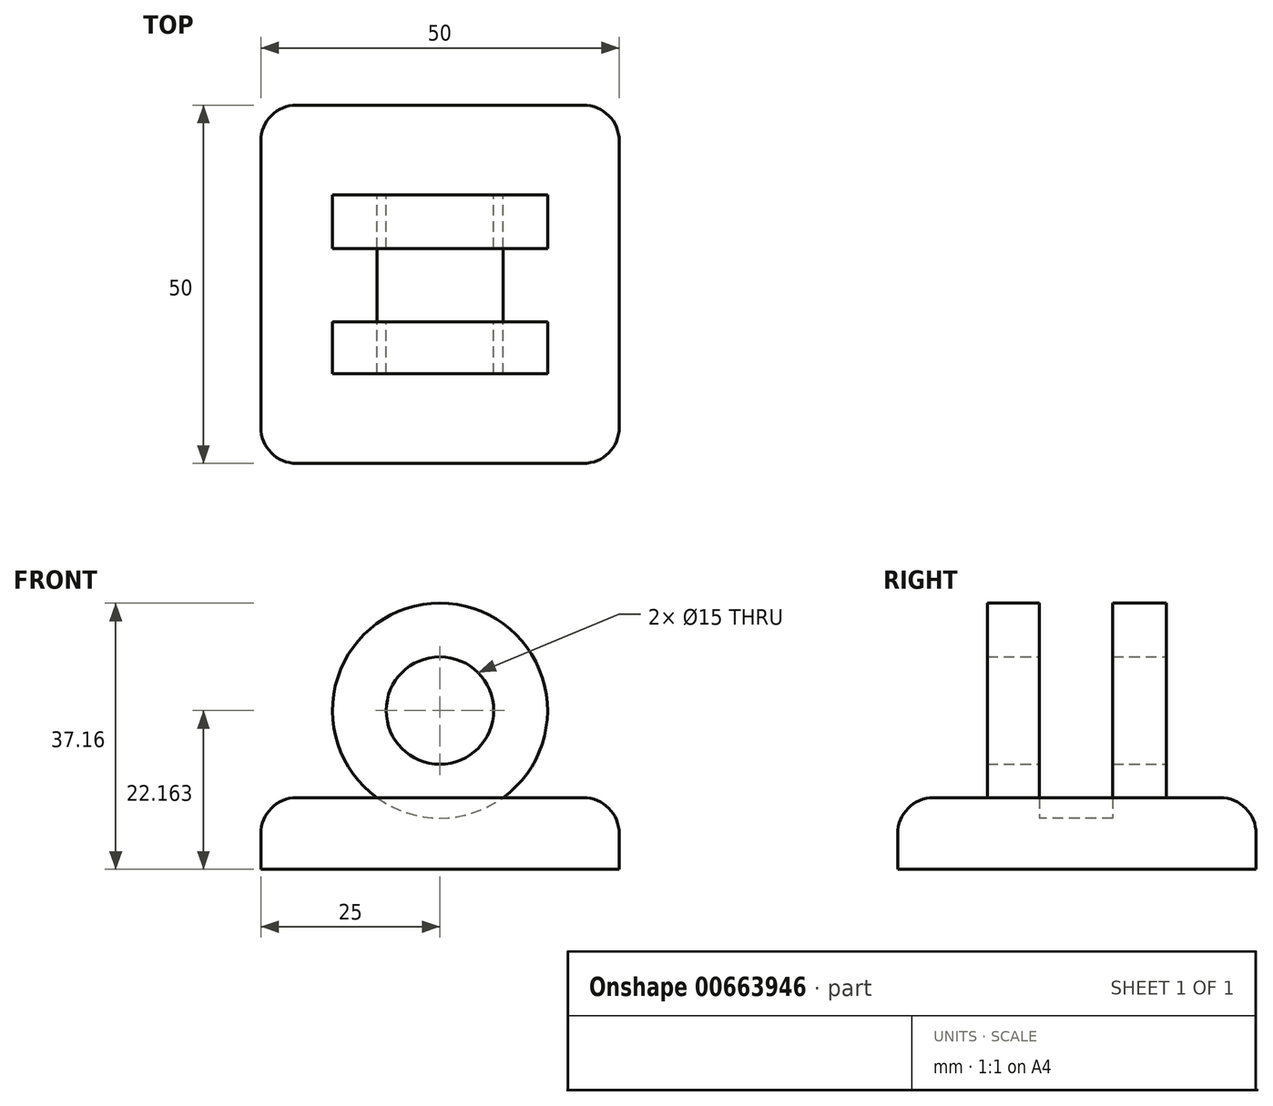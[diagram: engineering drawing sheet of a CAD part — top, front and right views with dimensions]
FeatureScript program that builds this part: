
annotation { "Feature Type Name" : "Feature", "Feature Type Description" : "" }
export const myFeature = defineFeature(function(context is Context, id is Id, definition is map)
    precondition{}
    {
        {
            var Q0;
            Q0=qCreatedBy(makeId("Top.planeOp"),FACE);
            var sketch = newSketch(context, id + "F0", { "sketchPlane" : qUnion([Q0])});
            skLineSegment(sketch, "E0.bottom", {"start": v(-25, -25) * mm, "end": v(25, -25) * mm});
            skLineSegment(sketch, "E0.top", {"start": v(-25, 25) * mm, "end": v(25, 25) * mm});
            skLineSegment(sketch, "E0.left", {"start": v(-25, -25) * mm, "end": v(-25, 25) * mm});
            skLineSegment(sketch, "E0.right", {"start": v(25, -25) * mm, "end": v(25, 25) * mm});
            skPoint(sketch, "E0.middle", {"position": v(0, 0) * mm});
            skSolve(sketch);
        }
        {
            var Q0;
            Q0=makeQuery(id+"F0.imprint","IMPRINT",FACE,{"disambiguationData":[TD([[makeQuery(id+"F0.imprint","IMPRINT",EDGE,{"derivedFrom":sQuery(id+"F0.wireOp",EDGE,"E0.bottom")}),1.0]])]});
            extrude(context, id + "F1", {"entities" : qUnion([Q0]), "depth" : 10 * mm, "offsetDistance" : 25 * mm});
        }
        {
            var Q0;
            Q0=makeQuery(id+"F1.opExtrude","SWEPT_EDGE",EDGE,{"disambiguationData":[OSD([sQuery(id+"F0.wireOp",EDGE,"E0.bottom"),sQuery(id+"F0.wireOp",EDGE,"E0.left")])]});
            fillet(context, id + "F2", {"entities" : qUnion([Q0]), "radius" : 5 * mm, "tangentPropagation" : true, "allowEdgeOverflow" : false});
        }
        {
            var Q0;
            Q0=makeQuery(id+"F1.opExtrude","SWEPT_EDGE",EDGE,{"disambiguationData":[OSD([sQuery(id+"F0.wireOp",EDGE,"E0.bottom"),sQuery(id+"F0.wireOp",EDGE,"E0.right")])]});
            var Q1;
            Q1=makeQuery(id+"F1.opExtrude","SWEPT_EDGE",EDGE,{"disambiguationData":[OSD([sQuery(id+"F0.wireOp",EDGE,"E0.top"),sQuery(id+"F0.wireOp",EDGE,"E0.left")])]});
            var Q2;
            Q2=makeQuery(id+"F1.opExtrude","SWEPT_EDGE",EDGE,{"disambiguationData":[OSD([sQuery(id+"F0.wireOp",EDGE,"E0.top"),sQuery(id+"F0.wireOp",EDGE,"E0.right")])]});
            var Q3;
            Q3=makeQuery(id+"F1.opExtrude","CAP_EDGE",EDGE,{"disambiguationData":[OSD([sQuery(id+"F0.wireOp",EDGE,"E0.top")])],"isStart":false});
            var Q4;
            Q4=makeQuery(id+"F1.opExtrude","CAP_EDGE",EDGE,{"disambiguationData":[OSD([sQuery(id+"F0.wireOp",EDGE,"E0.right")])],"isStart":false});
            var Q5;
            Q5=makeQuery(id+"F1.opExtrude","CAP_EDGE",EDGE,{"disambiguationData":[OSD([sQuery(id+"F0.wireOp",EDGE,"E0.bottom")])],"isStart":false});
            var Q6;
            Q6=makeQuery(id+"F1.opExtrude","CAP_EDGE",EDGE,{"disambiguationData":[OSD([sQuery(id+"F0.wireOp",EDGE,"E0.left")])],"isStart":false});
            fillet(context, id + "F3", {"entities" : qUnion([Q0, Q1, Q2, Q3, Q4, Q5, Q6]), "radius" : 5 * mm, "tangentPropagation" : true, "allowEdgeOverflow" : false});
        }
        {
            var Q0;
            Q0=qCreatedBy(makeId("Front.planeOp"),FACE);
            var sketch = newSketch(context, id + "F4", { "sketchPlane" : qUnion([Q0])});
            skCircle(sketch, "E1", {"center": v(0, 22.16) * mm, "radius": 15 * mm});
            skCircle(sketch, "E2", {"center": v(0, 22.16) * mm, "radius": 7.5 * mm});
            skSolve(sketch);
        }
        {
            var Q0;
            Q0=makeQuery(id+"F4.imprint","IMPRINT",FACE,{"disambiguationData":[TD([[makeQuery(id+"F4.imprint","IMPRINT",EDGE,{"derivedFrom":sQuery(id+"F4.wireOp",EDGE,"E1")}),1.0]])]});
            extrude(context, id + "F5", {"entities" : qUnion([Q0]), "operationType" : NewBodyOperationType.ADD, "depth" : 12.5 * mm, "offsetDistance" : 25 * mm, "hasSecondDirection" : true, "secondDirectionOppositeDirection" : true, "secondDirectionDepth" : 12.5 * mm});
        }
        {
            var Q0;
            Q0 = qSketchRegion(id + "F4", true);
            extrude(context, id + "F6", {"entities" : qUnion([Q0]), "operationType" : NewBodyOperationType.REMOVE, "oppositeDirection" : true, "depth" : 5 * mm, "offsetDistance" : 25 * mm, "hasSecondDirection" : true, "secondDirectionOppositeDirection" : false, "secondDirectionDepth" : 5.25 * mm});
        }
    });
